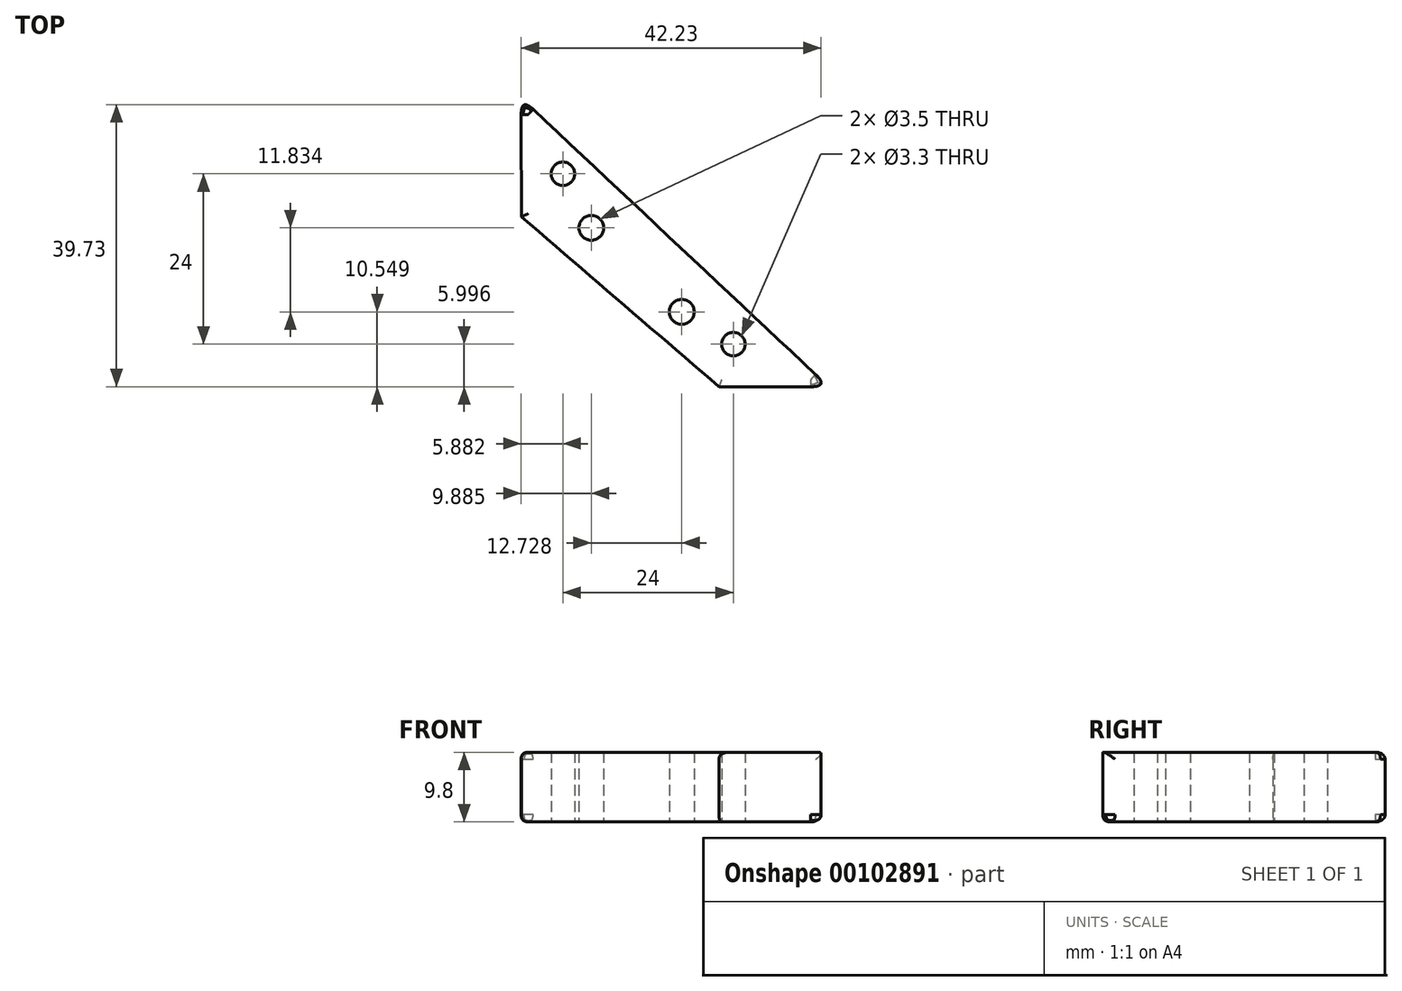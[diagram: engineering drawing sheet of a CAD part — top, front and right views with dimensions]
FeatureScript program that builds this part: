
annotation { "Feature Type Name" : "Feature", "Feature Type Description" : "" }
export const myFeature = defineFeature(function(context is Context, id is Id, definition is map)
    precondition{}
    {
        {
            var Q0;
            Q0=qCreatedBy(makeId("Top.planeOp"),FACE);
            var sketch = newSketch(context, id + "F0", { "sketchPlane" : qUnion([Q0])});
            skCircle(sketch, "E0.0", {"center": v(-44.1, -6.31) * mm, "radius": 3 * mm});
            skCircle(sketch, "E0.1", {"center": v(-108.1, -70.31) * mm, "radius": 3 * mm});
            skCircle(sketch, "E0.2", {"center": v(-108.1, -6.31) * mm, "radius": 3 * mm});
            skLineSegment(sketch, "E0.3", {"start": v(-117.1, -85.31) * mm, "end": v(-117.1, -55.31) * mm});
            skLineSegment(sketch, "E0.4", {"start": v(-123.1, -79.31) * mm, "end": v(-93.1, -79.31) * mm});
            skLineSegment(sketch, "E0.5", {"start": v(-29.1, -85.31) * mm, "end": v(-123.1, 8.69) * mm});
            skLineSegment(sketch, "E0.6", {"start": v(-108.1, -70.31) * mm, "end": v(-44.1, -70.31) * mm});
            skLineSegment(sketch, "E0.7", {"start": v(-108.1, -6.31) * mm, "end": v(-44.1, -6.31) * mm});
            skLineSegment(sketch, "E0.8", {"start": v(-108.1, -70.31) * mm, "end": v(-108.1, -6.31) * mm});
            skLineSegment(sketch, "E0.9", {"start": v(-44.1, -70.31) * mm, "end": v(-44.1, -6.31) * mm});
            skCircle(sketch, "E0.10", {"center": v(-44.1, -70.31) * mm, "radius": 3 * mm});
            skLineSegment(sketch, "E0.11", {"start": v(-44.1, -6.31) * mm, "end": v(-59.1, -6.31) * mm});
            skLineSegment(sketch, "E0.12", {"start": v(-44.1, -6.31) * mm, "end": v(-44.1, -21.31) * mm});
            skLineSegment(sketch, "E0.13", {"start": v(-89.92, 10.8) * mm, "end": v(-105.52, -4.8) * mm});
            skLineSegment(sketch, "E0.14", {"start": v(-89.92, 10.8) * mm, "end": v(-26.99, -52.12) * mm});
            skLineSegment(sketch, "E0.15", {"start": v(-125.23, -24.5) * mm, "end": v(-62.3, -87.44) * mm});
            skLineSegment(sketch, "E0.16", {"start": v(-109.63, -8.9) * mm, "end": v(-125.23, -24.5) * mm});
            skLineSegment(sketch, "E0.17", {"start": v(-123.1, 0.69) * mm, "end": v(-123.1, -77.31) * mm});
            skLineSegment(sketch, "E0.18", {"start": v(-51.74, -76.87) * mm, "end": v(-62.3, -87.44) * mm});
            skLineSegment(sketch, "E0.19", {"start": v(-29.1, 0.69) * mm, "end": v(-29.1, -77.31) * mm});
            skLineSegment(sketch, "E0.20", {"start": v(-115.1, 8.69) * mm, "end": v(-37.1, 8.69) * mm});
            skLineSegment(sketch, "E0.21", {"start": v(-115.1, -85.31) * mm, "end": v(-37.1, -85.31) * mm});
            skLineSegment(sketch, "E0.22", {"start": v(-123.1, -38.31) * mm, "end": v(-29.1, -38.31) * mm});
            skLineSegment(sketch, "E0.23", {"start": v(-44.1, -21.31) * mm, "end": v(-59.1, -6.31) * mm});
            skLineSegment(sketch, "E0.24", {"start": v(-76.1, -85.31) * mm, "end": v(-76.1, 8.69) * mm});
            skLineSegment(sketch, "E0.25", {"start": v(-44.1, -6.31) * mm, "end": v(-51.88, -13.54) * mm});
            skCircle(sketch, "E0.26", {"center": v(-66.3, -0.24) * mm, "radius": 1.75 * mm});
            skCircle(sketch, "E0.27", {"center": v(-63.1, -70.31) * mm, "radius": 1.75 * mm});
            skCircle(sketch, "E0.28", {"center": v(-85.9, -0.24) * mm, "radius": 1.75 * mm});
            skCircle(sketch, "E0.29", {"center": v(-51.5, -1.32) * mm, "radius": 1.75 * mm});
            skCircle(sketch, "E0.30", {"center": v(-63.1, -55.31) * mm, "radius": 1.75 * mm});
            skCircle(sketch, "E0.31", {"center": v(-78.1, -55.31) * mm, "radius": 1.75 * mm});
            skCircle(sketch, "E0.32", {"center": v(-85.53, -74.76) * mm, "radius": 1.75 * mm});
            skCircle(sketch, "E0.33", {"center": v(-78.1, -40.31) * mm, "radius": 1.75 * mm});
            skCircle(sketch, "E0.34", {"center": v(-35.1, -21.31) * mm, "radius": 1.65 * mm});
            skCircle(sketch, "E0.35", {"center": v(-59.1, 2.69) * mm, "radius": 1.65 * mm});
            skCircle(sketch, "E0.36", {"center": v(-100.38, -74.76) * mm, "radius": 1.75 * mm});
            skCircle(sketch, "E0.37", {"center": v(-78.1, -70.31) * mm, "radius": 1.75 * mm});
            skCircle(sketch, "E0.38", {"center": v(-113.1, -62.93) * mm, "radius": 1.75 * mm});
            skCircle(sketch, "E0.39", {"center": v(-93.1, -55.31) * mm, "radius": 1.75 * mm});
            skCircle(sketch, "E0.40", {"center": v(-93.1, -70.31) * mm, "radius": 1.75 * mm});
            skCircle(sketch, "E0.41", {"center": v(-89.1, -21.31) * mm, "radius": 1.75 * mm});
            skCircle(sketch, "E0.42", {"center": v(-39.66, -14.04) * mm, "radius": 1.75 * mm});
            skCircle(sketch, "E0.43", {"center": v(-44.1, -36.31) * mm, "radius": 1.75 * mm});
            skCircle(sketch, "E0.44", {"center": v(-44.1, -51.31) * mm, "radius": 1.75 * mm});
            skCircle(sketch, "E0.45", {"center": v(-59.1, -21.31) * mm, "radius": 1.75 * mm});
            skCircle(sketch, "E0.46", {"center": v(-59.1, -36.31) * mm, "radius": 1.75 * mm});
            skCircle(sketch, "E0.47", {"center": v(-59.1, -51.31) * mm, "radius": 1.75 * mm});
            skCircle(sketch, "E0.48", {"center": v(-74.1, -6.31) * mm, "radius": 1.75 * mm});
            skCircle(sketch, "E0.49", {"center": v(-74.1, -21.31) * mm, "radius": 1.75 * mm});
            skCircle(sketch, "E0.50", {"center": v(-74.1, -36.31) * mm, "radius": 1.75 * mm});
            skCircle(sketch, "E0.51", {"center": v(-89.1, -6.31) * mm, "radius": 1.75 * mm});
            skLineSegment(sketch, "E0.52", {"start": v(-123.1, 0.69) * mm, "end": v(-123.1, -77.31) * mm});
            skCircle(sketch, "E0.53", {"center": v(-108.1, -55.31) * mm, "radius": 1.75 * mm});
            skLineSegment(sketch, "E0.54", {"start": v(-115.1, 8.69) * mm, "end": v(-37.1, 8.69) * mm});
            skLineSegment(sketch, "E0.55", {"start": v(-30.18, -55.3) * mm, "end": v(-26.99, -52.12) * mm});
            skLineSegment(sketch, "E0.56", {"start": v(-115.1, -85.31) * mm, "end": v(-37.1, -85.31) * mm});
            skCircle(sketch, "E0.57", {"center": v(-93.1, -40.31) * mm, "radius": 1.75 * mm});
            skCircle(sketch, "E0.58", {"center": v(-39.66, -28.9) * mm, "radius": 1.75 * mm});
            skCircle(sketch, "E0.59", {"center": v(-39.66, -47.73) * mm, "radius": 1.75 * mm});
            skCircle(sketch, "E0.60", {"center": v(-93.1, -25.31) * mm, "radius": 1.75 * mm});
            skCircle(sketch, "E0.61", {"center": v(-66.3, -76.4) * mm, "radius": 1.75 * mm});
            skCircle(sketch, "E0.62", {"center": v(-108.1, -25.31) * mm, "radius": 1.75 * mm});
            skCircle(sketch, "E0.63", {"center": v(-112.55, -28.9) * mm, "radius": 1.75 * mm});
            skLineSegment(sketch, "E0.64", {"start": v(-29.1, 0.69) * mm, "end": v(-29.1, -77.31) * mm});
            skArc(sketch, "E0.65", {"start": v(-37.1, -85.31) * mm, "mid": v(-31.45, -82.97) * mm, "end": v(-29.1, -77.31) * mm});
            skArc(sketch, "E0.66", {"start": v(-29.1, 0.69) * mm, "mid": v(-31.45, 6.34) * mm, "end": v(-37.1, 8.69) * mm});
            skArc(sketch, "E0.67", {"start": v(-122.92, -75.58) * mm, "mid": v(-121.35, -82.32) * mm, "end": v(-115.1, -85.31) * mm});
            skLineSegment(sketch, "E0.68", {"start": v(-93.75, -60.52) * mm, "end": v(-88.1, -66.18) * mm});
            skCircle(sketch, "E0.69", {"center": v(-93.1, -79.31) * mm, "radius": 1.65 * mm});
            skCircle(sketch, "E0.70", {"center": v(-117.1, -55.31) * mm, "radius": 1.65 * mm});
            skCircle(sketch, "E0.71", {"center": v(-114.19, -48.11) * mm, "radius": 1.75 * mm});
            skLineSegment(sketch, "E0.72", {"start": v(-123.1, -24.5) * mm, "end": v(-123.82, -24.5) * mm});
            skCircle(sketch, "E0.73", {"center": v(-108.1, -40.31) * mm, "radius": 1.75 * mm});
            skArc(sketch, "E0.75", {"start": v(-29.1, -77.31) * mm, "mid": v(-31.45, -82.97) * mm, "end": v(-37.1, -85.31) * mm});
            skArc(sketch, "E0.76", {"start": v(-115.1, 8.69) * mm, "mid": v(-120.76, 6.34) * mm, "end": v(-123.1, 0.69) * mm});
            skLineSegment(sketch, "E0.78", {"start": v(-115.1, 8.69) * mm, "end": v(-37.1, 8.69) * mm});
            skLineSegment(sketch, "E0.79", {"start": v(-115.1, -85.31) * mm, "end": v(-37.1, -85.31) * mm});
            skLineSegment(sketch, "E0.80", {"start": v(-123.1, 0.69) * mm, "end": v(-122.92, -75.58) * mm});
            skLineSegment(sketch, "E0.81", {"start": v(-29.1, 0.69) * mm, "end": v(-29.1, -77.31) * mm});
            skCircle(sketch, "E0.82", {"center": v(-114.19, -48.11) * mm, "radius": 1.75 * mm});
            skCircle(sketch, "E0.83", {"center": v(-44.1, -21.31) * mm, "radius": 1.75 * mm});
            skCircle(sketch, "E0.84", {"center": v(-59.1, -6.31) * mm, "radius": 1.75 * mm});
            skCircle(sketch, "E0.85", {"center": v(-108.1, -40.31) * mm, "radius": 1.75 * mm});
            skCircle(sketch, "E0.86", {"center": v(-39.66, -28.9) * mm, "radius": 1.75 * mm});
            skCircle(sketch, "E0.87", {"center": v(-113.1, -62.93) * mm, "radius": 1.75 * mm});
            skArc(sketch, "E0.90", {"start": v(-123.1, 0.69) * mm, "mid": v(-120.76, 6.34) * mm, "end": v(-115.1, 8.69) * mm});
            skArc(sketch, "E0.92", {"start": v(-37.1, 8.69) * mm, "mid": v(-31.45, 6.34) * mm, "end": v(-29.1, 0.69) * mm});
            skArc(sketch, "E0.95", {"start": v(-115.1, -85.31) * mm, "mid": v(-121.35, -82.32) * mm, "end": v(-122.92, -75.58) * mm});
            skCircle(sketch, "E0.97", {"center": v(-63.1, -70.31) * mm, "radius": 1.75 * mm});
            skCircle(sketch, "E0.98", {"center": v(-63.1, -55.31) * mm, "radius": 1.75 * mm});
            skCircle(sketch, "E0.99", {"center": v(-39.66, -14.04) * mm, "radius": 1.75 * mm});
            skCircle(sketch, "E0.100", {"center": v(-44.1, -36.31) * mm, "radius": 1.75 * mm});
            skCircle(sketch, "E0.101", {"center": v(-44.1, -51.31) * mm, "radius": 1.75 * mm});
            skCircle(sketch, "E0.102", {"center": v(-66.3, -76.4) * mm, "radius": 1.75 * mm});
            skCircle(sketch, "E0.103", {"center": v(-78.1, -70.31) * mm, "radius": 1.75 * mm});
            skCircle(sketch, "E0.104", {"center": v(-74.1, -36.31) * mm, "radius": 1.75 * mm});
            skCircle(sketch, "E0.105", {"center": v(-89.1, -6.31) * mm, "radius": 1.75 * mm});
            skCircle(sketch, "E0.106", {"center": v(-89.1, -21.31) * mm, "radius": 1.75 * mm});
            skLineSegment(sketch, "E0.107", {"start": v(-115.1, 8.69) * mm, "end": v(-37.1, 8.69) * mm});
            skLineSegment(sketch, "E0.108", {"start": v(-115.1, -85.31) * mm, "end": v(-37.1, -85.31) * mm});
            skLineSegment(sketch, "E0.109", {"start": v(-123.1, 0.69) * mm, "end": v(-122.92, -75.58) * mm});
            skLineSegment(sketch, "E0.110", {"start": v(-89.6, -67.69) * mm, "end": v(-87.36, -67.69) * mm});
            skLineSegment(sketch, "E0.116", {"start": v(-94.53, -61.3) * mm, "end": v(-88.87, -66.96) * mm});
            skCircle(sketch, "E0.117", {"center": v(-108.1, -70.31) * mm, "radius": 1.75 * mm});
            skCircle(sketch, "E0.118", {"center": v(-44.1, -70.31) * mm, "radius": 1.65 * mm});
            skCircle(sketch, "E0.119", {"center": v(-108.1, -6.31) * mm, "radius": 1.65 * mm});
            skCircle(sketch, "E0.120", {"center": v(-39.66, -14.04) * mm, "radius": 1.75 * mm});
            skCircle(sketch, "E0.121", {"center": v(-66.3, -76.4) * mm, "radius": 1.75 * mm});
            skCircle(sketch, "E0.122", {"center": v(-78.1, -70.31) * mm, "radius": 1.75 * mm});
            skCircle(sketch, "E0.123", {"center": v(-66.3, -0.24) * mm, "radius": 1.75 * mm});
            skCircle(sketch, "E0.124", {"center": v(-44.1, -36.31) * mm, "radius": 1.75 * mm});
            skCircle(sketch, "E0.125", {"center": v(-100.38, -74.76) * mm, "radius": 1.75 * mm});
            skCircle(sketch, "E0.126", {"center": v(-44.1, -51.31) * mm, "radius": 1.75 * mm});
            skLineSegment(sketch, "E0.127", {"start": v(-94.53, -61.3) * mm, "end": v(-88.87, -66.96) * mm});
            skCircle(sketch, "E0.128", {"center": v(-85.53, -74.76) * mm, "radius": 1.75 * mm});
            skCircle(sketch, "E0.129", {"center": v(-35.1, -21.31) * mm, "radius": 1.65 * mm});
            skCircle(sketch, "E0.130", {"center": v(-78.1, -55.31) * mm, "radius": 1.75 * mm});
            skCircle(sketch, "E0.131", {"center": v(-39.66, -28.9) * mm, "radius": 1.75 * mm});
            skCircle(sketch, "E0.132", {"center": v(-59.1, -21.31) * mm, "radius": 1.75 * mm});
            skCircle(sketch, "E0.133", {"center": v(-59.1, -36.31) * mm, "radius": 1.75 * mm});
            skCircle(sketch, "E0.134", {"center": v(-59.1, -51.31) * mm, "radius": 1.75 * mm});
            skCircle(sketch, "E0.135", {"center": v(-74.1, -6.31) * mm, "radius": 1.75 * mm});
            skCircle(sketch, "E0.136", {"center": v(-74.1, -21.31) * mm, "radius": 1.75 * mm});
            skCircle(sketch, "E0.137", {"center": v(-74.1, -36.31) * mm, "radius": 1.75 * mm});
            skCircle(sketch, "E0.138", {"center": v(-112.55, -28.9) * mm, "radius": 1.75 * mm});
            skCircle(sketch, "E0.139", {"center": v(-89.1, -6.31) * mm, "radius": 1.75 * mm});
            skCircle(sketch, "E0.140", {"center": v(-89.1, -21.31) * mm, "radius": 1.75 * mm});
            skCircle(sketch, "E0.141", {"center": v(-63.1, -70.31) * mm, "radius": 1.75 * mm});
            skCircle(sketch, "E0.142", {"center": v(-63.1, -55.31) * mm, "radius": 1.75 * mm});
            skCircle(sketch, "E0.143", {"center": v(-113.1, -62.93) * mm, "radius": 1.75 * mm});
            skLineSegment(sketch, "E0.144", {"start": v(-93.75, -60.52) * mm, "end": v(-88.1, -66.18) * mm});
            skLineSegment(sketch, "E0.147", {"start": v(-88.1, -66.18) * mm, "end": v(-87.36, -65.45) * mm});
            skLineSegment(sketch, "E0.148", {"start": v(-93.75, -60.52) * mm, "end": v(-94.53, -61.3) * mm});
            skLineSegment(sketch, "E0.149", {"start": v(-88.87, -66.96) * mm, "end": v(-89.6, -67.69) * mm});
            skCircle(sketch, "E0.150", {"center": v(-108.1, -25.31) * mm, "radius": 1.75 * mm});
            skLineSegment(sketch, "E0.151", {"start": v(-93.75, -60.52) * mm, "end": v(-94.53, -61.3) * mm});
            skCircle(sketch, "E0.152", {"center": v(-112.55, -28.9) * mm, "radius": 1.75 * mm});
            skCircle(sketch, "E0.153", {"center": v(-59.1, -21.31) * mm, "radius": 1.75 * mm});
            skCircle(sketch, "E0.154", {"center": v(-51.5, -1.32) * mm, "radius": 1.75 * mm});
            skCircle(sketch, "E0.155", {"center": v(-59.1, -36.31) * mm, "radius": 1.75 * mm});
            skLineSegment(sketch, "E0.156", {"start": v(-88.87, -66.96) * mm, "end": v(-89.6, -67.69) * mm});
            skCircle(sketch, "E0.157", {"center": v(-59.1, -51.31) * mm, "radius": 1.75 * mm});
            skCircle(sketch, "E0.158", {"center": v(-114.19, -48.11) * mm, "radius": 1.75 * mm});
            skCircle(sketch, "E0.159", {"center": v(-35.1, -21.31) * mm, "radius": 1.65 * mm});
            skCircle(sketch, "E0.160", {"center": v(-44.1, -70.31) * mm, "radius": 3 * mm});
            skCircle(sketch, "E0.161", {"center": v(-108.1, -6.31) * mm, "radius": 3 * mm});
            skCircle(sketch, "E0.162", {"center": v(-44.1, -6.31) * mm, "radius": 3 * mm});
            skCircle(sketch, "E0.163", {"center": v(-108.1, -70.31) * mm, "radius": 3 * mm});
            skCircle(sketch, "E0.164", {"center": v(-74.1, -6.31) * mm, "radius": 1.75 * mm});
            skCircle(sketch, "E0.165", {"center": v(-39.66, -47.73) * mm, "radius": 1.75 * mm});
            skCircle(sketch, "E0.166", {"center": v(-78.1, -40.31) * mm, "radius": 1.75 * mm});
            skCircle(sketch, "E0.167", {"center": v(-44.1, -21.31) * mm, "radius": 1.75 * mm});
            skCircle(sketch, "E0.168", {"center": v(-74.1, -21.31) * mm, "radius": 1.75 * mm});
            skCircle(sketch, "E0.169", {"center": v(-93.1, -55.31) * mm, "radius": 1.75 * mm});
            skCircle(sketch, "E0.170", {"center": v(-66.3, -0.24) * mm, "radius": 1.75 * mm});
            skCircle(sketch, "E0.171", {"center": v(-85.9, -0.24) * mm, "radius": 1.75 * mm});
            skCircle(sketch, "E0.172", {"center": v(-93.1, -70.31) * mm, "radius": 1.75 * mm});
            skCircle(sketch, "E0.173", {"center": v(-108.1, -55.31) * mm, "radius": 1.75 * mm});
            skCircle(sketch, "E0.174", {"center": v(-85.53, -74.76) * mm, "radius": 1.75 * mm});
            skCircle(sketch, "E0.175", {"center": v(-93.1, -40.31) * mm, "radius": 1.75 * mm});
            skCircle(sketch, "E0.176", {"center": v(-100.38, -74.76) * mm, "radius": 1.75 * mm});
            skCircle(sketch, "E0.177", {"center": v(-93.1, -25.31) * mm, "radius": 1.75 * mm});
            skCircle(sketch, "E0.178", {"center": v(-78.1, -55.31) * mm, "radius": 1.75 * mm});
            skLineSegment(sketch, "E0.179", {"start": v(-87.36, -65.45) * mm, "end": v(-87.36, -67.69) * mm});
            skCircle(sketch, "E0.180", {"center": v(-44.1, -21.31) * mm, "radius": 1.75 * mm});
            skLineSegment(sketch, "E0.181", {"start": v(-87.36, -65.45) * mm, "end": v(-87.36, -67.69) * mm});
            skCircle(sketch, "E0.182", {"center": v(-59.1, 2.69) * mm, "radius": 1.65 * mm});
            skLineSegment(sketch, "E0.183", {"start": v(-89.6, -67.69) * mm, "end": v(-87.36, -67.69) * mm});
            skCircle(sketch, "E0.184", {"center": v(-59.1, -6.31) * mm, "radius": 1.75 * mm});
            skCircle(sketch, "E0.185", {"center": v(-114.19, -48.11) * mm, "radius": 1.75 * mm});
            skLineSegment(sketch, "E0.186", {"start": v(-88.1, -66.18) * mm, "end": v(-87.36, -65.45) * mm});
            skCircle(sketch, "E0.187", {"center": v(-39.66, -47.73) * mm, "radius": 1.75 * mm});
            skCircle(sketch, "E0.188", {"center": v(-78.1, -40.31) * mm, "radius": 1.75 * mm});
            skCircle(sketch, "E0.189", {"center": v(-93.1, -55.31) * mm, "radius": 1.75 * mm});
            skCircle(sketch, "E0.190", {"center": v(-93.1, -40.31) * mm, "radius": 1.75 * mm});
            skCircle(sketch, "E0.191", {"center": v(-85.9, -0.24) * mm, "radius": 1.75 * mm});
            skCircle(sketch, "E0.192", {"center": v(-93.1, -70.31) * mm, "radius": 1.75 * mm});
            skCircle(sketch, "E0.193", {"center": v(-108.1, -55.31) * mm, "radius": 1.75 * mm});
            skCircle(sketch, "E0.194", {"center": v(-59.1, -6.31) * mm, "radius": 1.75 * mm});
            skCircle(sketch, "E0.195", {"center": v(-93.1, -79.31) * mm, "radius": 1.65 * mm});
            skCircle(sketch, "E0.196", {"center": v(-117.1, -55.31) * mm, "radius": 1.65 * mm});
            skCircle(sketch, "E0.197", {"center": v(-93.1, -25.31) * mm, "radius": 1.75 * mm});
            skCircle(sketch, "E0.198", {"center": v(-44.1, -70.31) * mm, "radius": 1.65 * mm});
            skCircle(sketch, "E0.199", {"center": v(-44.1, -70.31) * mm, "radius": 3 * mm});
            skCircle(sketch, "E0.200", {"center": v(-108.1, -70.31) * mm, "radius": 1.75 * mm});
            skCircle(sketch, "E0.201", {"center": v(-108.1, -6.31) * mm, "radius": 3 * mm});
            skCircle(sketch, "E0.202", {"center": v(-108.1, -6.31) * mm, "radius": 1.65 * mm});
            skCircle(sketch, "E0.203", {"center": v(-44.1, -6.31) * mm, "radius": 3 * mm});
            skCircle(sketch, "E0.204", {"center": v(-108.1, -70.31) * mm, "radius": 3 * mm});
            skCircle(sketch, "E0.205", {"center": v(-108.1, -25.31) * mm, "radius": 1.75 * mm});
            skCircle(sketch, "E0.206", {"center": v(-51.5, -1.32) * mm, "radius": 1.75 * mm});
            skCircle(sketch, "E0.207", {"center": v(-108.1, -40.31) * mm, "radius": 1.75 * mm});
            skCircle(sketch, "E0.208", {"center": v(-44.1, -6.31) * mm, "radius": 1.75 * mm});
            skCircle(sketch, "E0.209", {"center": v(-59.1, 2.69) * mm, "radius": 1.65 * mm});
            skCircle(sketch, "E0.210", {"center": v(-44.1, -6.31) * mm, "radius": 1.75 * mm});
            skCircle(sketch, "E0.211", {"center": v(-108.1, -40.31) * mm, "radius": 1.75 * mm});
            skCircle(sketch, "E0.212", {"center": v(-108.1, -70.31) * mm, "radius": 1.75 * mm});
            skCircle(sketch, "E0.213", {"center": v(-108.1, -6.31) * mm, "radius": 1.65 * mm});
            skCircle(sketch, "E0.214", {"center": v(-93.1, -79.31) * mm, "radius": 1.65 * mm});
            skCircle(sketch, "E0.215", {"center": v(-117.1, -55.31) * mm, "radius": 1.65 * mm});
            skCircle(sketch, "E0.216", {"center": v(-44.1, -70.31) * mm, "radius": 1.65 * mm});
            skCircle(sketch, "E0.217", {"center": v(-44.1, -6.31) * mm, "radius": 1.75 * mm});
            skCircle(sketch, "E0.218", {"center": v(-44.1, -6.31) * mm, "radius": 1.75 * mm});
            skLineSegment(sketch, "E1", {"start": v(-123, -44.64) * mm, "end": v(-79.7, -85.31) * mm});
            skLineSegment(sketch, "E2", {"start": v(-95.13, -85.31) * mm, "end": v(-122.95, -61.37) * mm});
            skSolve(sketch);
        }
        {
            var Q0;
            Q0=qCreatedBy(makeId("Top.planeOp"),FACE);
            var sketch = newSketch(context, id + "F1", { "sketchPlane" : qUnion([Q0])});
            skLineSegment(sketch, "E3.0.2", {"start": v(-108.1, -58.62) * mm, "end": v(-123, -44.64) * mm});
            skLineSegment(sketch, "E3.0.3", {"start": v(-123, -44.64) * mm, "end": v(-122.95, -61.37) * mm});
            skLineSegment(sketch, "E3.0.4", {"start": v(-122.95, -61.37) * mm, "end": v(-117.1, -66.4) * mm});
            skLineSegment(sketch, "E3.0.5", {"start": v(-117.1, -66.4) * mm, "end": v(-110.57, -72.03) * mm});
            skLineSegment(sketch, "E3.1.2", {"start": v(-95.66, -70.31) * mm, "end": v(-108.1, -58.62) * mm});
            skLineSegment(sketch, "E3.2.2", {"start": v(-109.44, -73) * mm, "end": v(-102.1, -79.31) * mm});
            skLineSegment(sketch, "E3.2.3", {"start": v(-102.1, -79.31) * mm, "end": v(-95.13, -85.31) * mm});
            skLineSegment(sketch, "E3.2.4", {"start": v(-95.13, -85.31) * mm, "end": v(-79.7, -85.31) * mm});
            skLineSegment(sketch, "E3.2.5", {"start": v(-79.7, -85.31) * mm, "end": v(-94.3, -71.59) * mm});
            skLineSegment(sketch, "E3.2.6", {"start": v(-94.3, -71.59) * mm, "end": v(-95.66, -70.31) * mm});
            skCircle(sketch, "E4.0", {"center": v(-100.38, -74.76) * mm, "radius": 1.75 * mm});
            skCircle(sketch, "E4.1", {"center": v(-93.1, -79.31) * mm, "radius": 1.65 * mm});
            skCircle(sketch, "E4.2", {"center": v(-113.1, -62.93) * mm, "radius": 1.75 * mm});
            skCircle(sketch, "E4.3", {"center": v(-117.1, -55.31) * mm, "radius": 1.65 * mm});
            skLineSegment(sketch, "E5", {"start": v(-122.95, -61.37) * mm, "end": v(-95.13, -85.31) * mm});
            skPoint(sketch, "E3.0.1.start.orphan", {"position": v(-108.1, -67.31) * mm});
            skPoint(sketch, "E3.1.1.start.orphan", {"position": v(-105.1, -70.31) * mm});
            skSolve(sketch);
        }
        {
            var Q0;
            Q0 = qSketchRegion(id + "F1", true);
            extrude(context, id + "F2", {"entities" : qUnion([Q0]), "depth" : 9.8 * mm});
        }
        {
            var Q0;
            Q0=makeQuery(id+"F2.opExtrude","CAP_EDGE",EDGE,{"disambiguationData":[OSD([sQuery(id+"F1.wireOp",EDGE,"E5")])],"isStart":false});
            var Q1;
            Q1=makeQuery(id+"F2.opExtrude","SWEPT_EDGE",EDGE,{"disambiguationData":[OSD([sQuery(id+"F1.wireOp",EDGE,"E3.2.4"),sQuery(id+"F1.wireOp",EDGE,"E3.2.5")])]});
            var Q2;
            Q2=makeQuery(id+"F2.opExtrude","CAP_EDGE",EDGE,{"disambiguationData":[OSD([sQuery(id+"F1.wireOp",EDGE,"E3.0.3")])],"isStart":false});
            var Q3;
            Q3=makeQuery(id+"F2.opExtrude","SWEPT_EDGE",EDGE,{"disambiguationData":[OSD([sQuery(id+"F1.wireOp",EDGE,"E3.0.2"),sQuery(id+"F1.wireOp",EDGE,"E3.0.3")])]});
            var Q4;
            Q4=makeQuery(id+"F2.opExtrude","CAP_EDGE",EDGE,{"disambiguationData":[OSD([sQuery(id+"F1.wireOp",EDGE,"E3.0.3")])],"isStart":true});
            var Q5;
            Q5=makeQuery(id+"F2.opExtrude","CAP_EDGE",EDGE,{"disambiguationData":[OSD([sQuery(id+"F1.wireOp",EDGE,"E3.2.4")])],"isStart":true});
            var Q6;
            Q6=makeQuery(id+"F2.opExtrude","CAP_EDGE",EDGE,{"disambiguationData":[OSD([sQuery(id+"F1.wireOp",EDGE,"E5")])],"isStart":true});
            var Q7;
            Q7=makeQuery(id+"F2.opExtrude","CAP_EDGE",EDGE,{"disambiguationData":[OSD([sQuery(id+"F1.wireOp",EDGE,"E3.0.2"),sQuery(id+"F1.wireOp",EDGE,"E3.1.2"),sQuery(id+"F1.wireOp",EDGE,"E3.2.5"),sQuery(id+"F1.wireOp",EDGE,"E3.2.6")])],"isStart":false});
            var Q8;
            Q8=makeQuery(id+"F2.opExtrude","CAP_EDGE",EDGE,{"disambiguationData":[OSD([sQuery(id+"F1.wireOp",EDGE,"E3.0.2"),sQuery(id+"F1.wireOp",EDGE,"E3.1.2"),sQuery(id+"F1.wireOp",EDGE,"E3.2.5"),sQuery(id+"F1.wireOp",EDGE,"E3.2.6")])],"isStart":true});
            fillet(context, id + "F3", {"entities" : qUnion([Q0, Q1, Q2, Q3, Q4, Q5, Q6, Q7, Q8]), "radius" : 1 * mm, "tangentPropagation" : true, "rho" : 0.5, "crossSection" : FilletCrossSection.CONIC, "allowEdgeOverflow" : false});
        }
    });
